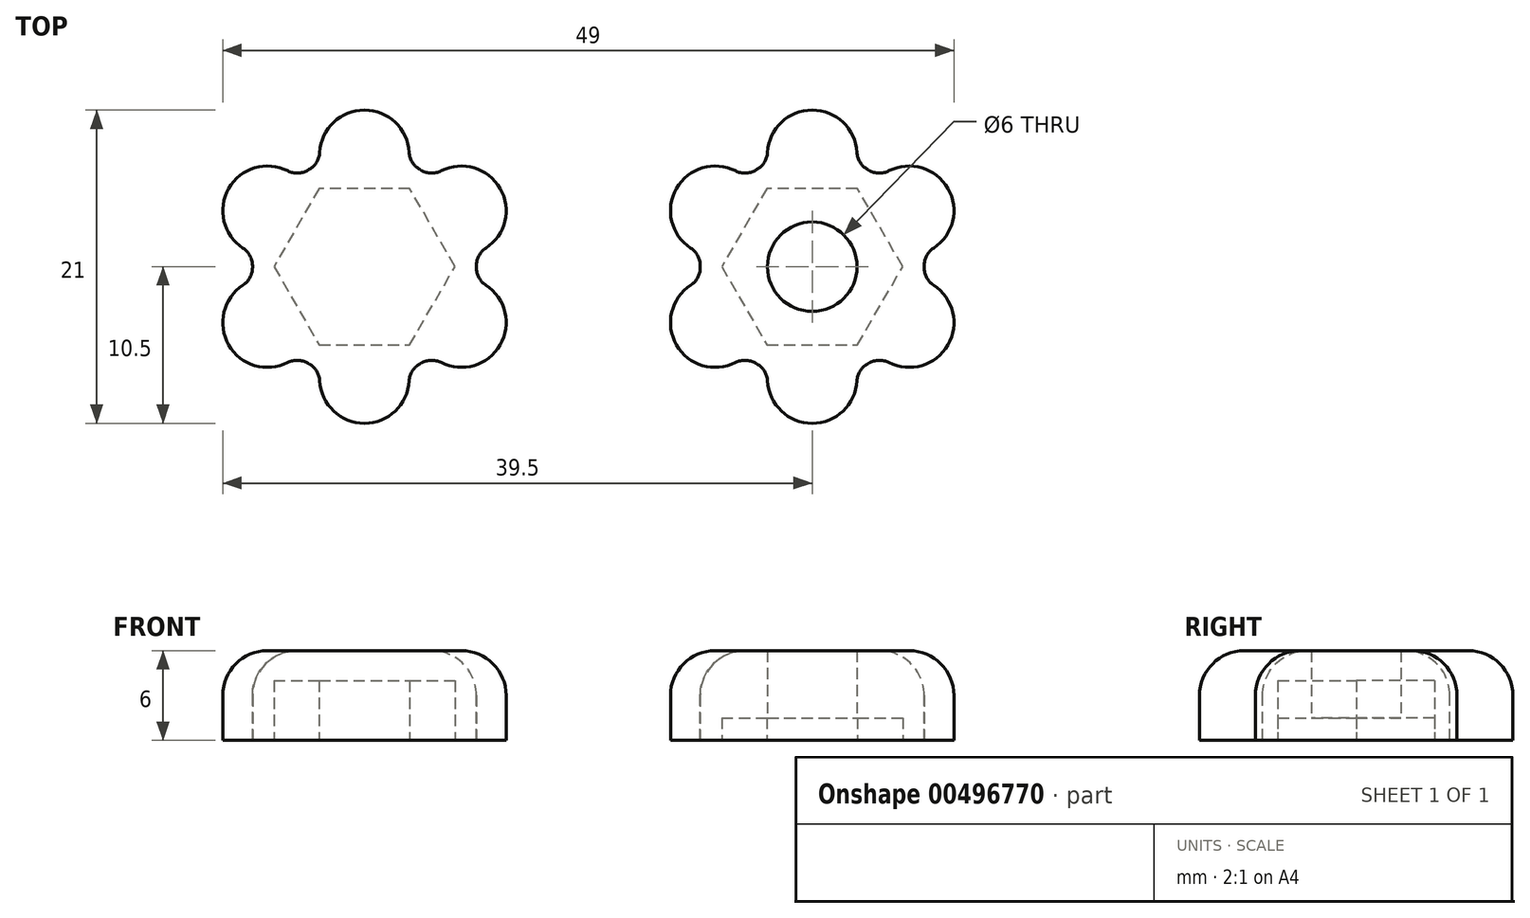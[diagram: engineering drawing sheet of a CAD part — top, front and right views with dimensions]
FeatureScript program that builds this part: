
annotation { "Feature Type Name" : "Feature", "Feature Type Description" : "" }
export const myFeature = defineFeature(function(context is Context, id is Id, definition is map)
    precondition{}
    {
        {
            var Q0;
            Q0=qCreatedBy(makeId("Top.planeOp"),FACE);
            var sketch = newSketch(context, id + "F0", { "sketchPlane" : qUnion([Q0])});
            skCircle(sketch, "E0", {"center": v(0, 0) * mm, "radius": 7.5 * mm});
            skCircle(sketch, "E1", {"center": v(0, 7.5) * mm, "radius": 3 * mm});
            skLineSegment(sketch, "E2", {"start": v(0, 0) * mm, "end": v(12.1, 6.98) * mm, "construction": true});
            skLineSegment(sketch, "E3", {"start": v(0, 0) * mm, "end": v(-10.24, 5.9) * mm, "construction": true});
            skLineSegment(sketch, "E4", {"start": v(-8.4, -4.85) * mm, "end": v(0, 0) * mm, "construction": true});
            skLineSegment(sketch, "E5", {"start": v(0, 0) * mm, "end": v(9.75, -5.63) * mm, "construction": true});
            skCircle(sketch, "E6", {"center": v(6.5, 3.75) * mm, "radius": 3 * mm});
            skCircle(sketch, "E7", {"center": v(6.5, -3.75) * mm, "radius": 3 * mm});
            skCircle(sketch, "E8", {"center": v(0, -7.5) * mm, "radius": 3 * mm});
            skCircle(sketch, "E9", {"center": v(-6.5, -3.75) * mm, "radius": 3 * mm});
            skCircle(sketch, "E10", {"center": v(-6.5, 3.75) * mm, "radius": 3 * mm});
            skSolve(sketch);
        }
        {
            var Q0;
            {var subQ0=sQuery(id+"F0.wireOp",EDGE,"E6");var subQ1=sQuery(id+"F0.wireOp",EDGE,"E0");var subQ11=makeQuery(id+"F0.imprint","INTERSECT",VERTEX,{"disambiguationData":[OD(0.0)],"derivedFrom":[subQ1,subQ0]});Q0=makeQuery(id+"F0.imprint","IMPRINT",FACE,{"disambiguationData":[TD([[makeQuery(id+"F0.imprint","IMPRINT",EDGE,{"disambiguationData":[TD([[subQ11,-1.0]])],"derivedFrom":subQ1}),1.0]])]});}
            var Q1;
            {var subQ0=sQuery(id+"F0.wireOp",EDGE,"E10");var subQ1=sQuery(id+"F0.wireOp",EDGE,"E0");var subQ2=makeQuery(id+"F0.imprint","INTERSECT",VERTEX,{"disambiguationData":[OD(0.0)],"derivedFrom":[subQ1,subQ0]});Q1=makeQuery(id+"F0.imprint","IMPRINT",FACE,{"disambiguationData":[TD([[makeQuery(id+"F0.imprint","IMPRINT",EDGE,{"disambiguationData":[TD([[subQ2,-1.0]])],"derivedFrom":subQ1}),1.0]])]});}
            var Q2;
            {var subQ0=sQuery(id+"F0.wireOp",EDGE,"E10");var subQ1=sQuery(id+"F0.wireOp",EDGE,"E0");var subQ2=makeQuery(id+"F0.imprint","INTERSECT",VERTEX,{"disambiguationData":[OD(0.0)],"derivedFrom":[subQ1,subQ0]});Q2=makeQuery(id+"F0.imprint","IMPRINT",FACE,{"disambiguationData":[TD([[makeQuery(id+"F0.imprint","IMPRINT",EDGE,{"disambiguationData":[TD([[subQ2,-1.0]])],"derivedFrom":subQ1}),-1.0]])]});}
            var Q3;
            {var subQ0=sQuery(id+"F0.wireOp",EDGE,"E1");var subQ1=sQuery(id+"F0.wireOp",EDGE,"E0");var subQ2=makeQuery(id+"F0.imprint","INTERSECT",VERTEX,{"disambiguationData":[OD(0.0)],"derivedFrom":[subQ1,subQ0]});Q3=makeQuery(id+"F0.imprint","IMPRINT",FACE,{"disambiguationData":[TD([[makeQuery(id+"F0.imprint","IMPRINT",EDGE,{"disambiguationData":[TD([[subQ2,-1.0]])],"derivedFrom":subQ1}),1.0]])]});}
            var Q4;
            {var subQ0=sQuery(id+"F0.wireOp",EDGE,"E6");var subQ1=sQuery(id+"F0.wireOp",EDGE,"E0");var subQ2=makeQuery(id+"F0.imprint","INTERSECT",VERTEX,{"disambiguationData":[OD(0.0)],"derivedFrom":[subQ1,subQ0]});Q4=makeQuery(id+"F0.imprint","IMPRINT",FACE,{"disambiguationData":[TD([[makeQuery(id+"F0.imprint","IMPRINT",EDGE,{"disambiguationData":[TD([[subQ2,1.0]])],"derivedFrom":subQ1}),1.0]])]});}
            var Q5;
            {var subQ0=sQuery(id+"F0.wireOp",EDGE,"E7");var subQ1=sQuery(id+"F0.wireOp",EDGE,"E0");var subQ2=makeQuery(id+"F0.imprint","INTERSECT",VERTEX,{"disambiguationData":[OD(0.0)],"derivedFrom":[subQ1,subQ0]});Q5=makeQuery(id+"F0.imprint","IMPRINT",FACE,{"disambiguationData":[TD([[makeQuery(id+"F0.imprint","IMPRINT",EDGE,{"disambiguationData":[TD([[subQ2,-1.0]])],"derivedFrom":subQ1}),1.0]])]});}
            var Q6;
            {var subQ0=sQuery(id+"F0.wireOp",EDGE,"E8");var subQ1=sQuery(id+"F0.wireOp",EDGE,"E0");var subQ2=makeQuery(id+"F0.imprint","INTERSECT",VERTEX,{"disambiguationData":[OD(0.0)],"derivedFrom":[subQ1,subQ0]});Q6=makeQuery(id+"F0.imprint","IMPRINT",FACE,{"disambiguationData":[TD([[makeQuery(id+"F0.imprint","IMPRINT",EDGE,{"disambiguationData":[TD([[subQ2,-1.0]])],"derivedFrom":subQ1}),1.0]])]});}
            var Q7;
            {var subQ0=sQuery(id+"F0.wireOp",EDGE,"E9");var subQ1=sQuery(id+"F0.wireOp",EDGE,"E0");var subQ2=makeQuery(id+"F0.imprint","INTERSECT",VERTEX,{"disambiguationData":[OD(0.0)],"derivedFrom":[subQ1,subQ0]});Q7=makeQuery(id+"F0.imprint","IMPRINT",FACE,{"disambiguationData":[TD([[makeQuery(id+"F0.imprint","IMPRINT",EDGE,{"disambiguationData":[TD([[subQ2,-1.0]])],"derivedFrom":subQ1}),1.0]])]});}
            var Q8;
            {var subQ0=sQuery(id+"F0.wireOp",EDGE,"E9");var subQ1=sQuery(id+"F0.wireOp",EDGE,"E0");var subQ2=makeQuery(id+"F0.imprint","INTERSECT",VERTEX,{"disambiguationData":[OD(0.0)],"derivedFrom":[subQ1,subQ0]});Q8=makeQuery(id+"F0.imprint","IMPRINT",FACE,{"disambiguationData":[TD([[makeQuery(id+"F0.imprint","IMPRINT",EDGE,{"disambiguationData":[TD([[subQ2,-1.0]])],"derivedFrom":subQ1}),-1.0]])]});}
            var Q9;
            {var subQ0=sQuery(id+"F0.wireOp",EDGE,"E8");var subQ1=sQuery(id+"F0.wireOp",EDGE,"E0");var subQ2=makeQuery(id+"F0.imprint","INTERSECT",VERTEX,{"disambiguationData":[OD(0.0)],"derivedFrom":[subQ1,subQ0]});Q9=makeQuery(id+"F0.imprint","IMPRINT",FACE,{"disambiguationData":[TD([[makeQuery(id+"F0.imprint","IMPRINT",EDGE,{"disambiguationData":[TD([[subQ2,-1.0]])],"derivedFrom":subQ1}),-1.0]])]});}
            var Q10;
            {var subQ0=sQuery(id+"F0.wireOp",EDGE,"E7");var subQ1=sQuery(id+"F0.wireOp",EDGE,"E0");var subQ2=makeQuery(id+"F0.imprint","INTERSECT",VERTEX,{"disambiguationData":[OD(0.0)],"derivedFrom":[subQ1,subQ0]});Q10=makeQuery(id+"F0.imprint","IMPRINT",FACE,{"disambiguationData":[TD([[makeQuery(id+"F0.imprint","IMPRINT",EDGE,{"disambiguationData":[TD([[subQ2,-1.0]])],"derivedFrom":subQ1}),-1.0]])]});}
            var Q11;
            {var subQ0=sQuery(id+"F0.wireOp",EDGE,"E6");var subQ1=sQuery(id+"F0.wireOp",EDGE,"E0");var subQ2=makeQuery(id+"F0.imprint","INTERSECT",VERTEX,{"disambiguationData":[OD(0.0)],"derivedFrom":[subQ1,subQ0]});Q11=makeQuery(id+"F0.imprint","IMPRINT",FACE,{"disambiguationData":[TD([[makeQuery(id+"F0.imprint","IMPRINT",EDGE,{"disambiguationData":[TD([[subQ2,1.0]])],"derivedFrom":subQ1}),-1.0]])]});}
            var Q12;
            {var subQ0=sQuery(id+"F0.wireOp",EDGE,"E1");var subQ1=sQuery(id+"F0.wireOp",EDGE,"E0");var subQ2=makeQuery(id+"F0.imprint","INTERSECT",VERTEX,{"disambiguationData":[OD(0.0)],"derivedFrom":[subQ1,subQ0]});Q12=makeQuery(id+"F0.imprint","IMPRINT",FACE,{"disambiguationData":[TD([[makeQuery(id+"F0.imprint","IMPRINT",EDGE,{"disambiguationData":[TD([[subQ2,-1.0]])],"derivedFrom":subQ1}),-1.0]])]});}
            extrude(context, id + "F1", {"entities" : qUnion([Q0, Q1, Q2, Q3, Q4, Q5, Q6, Q7, Q8, Q9, Q10, Q11, Q12]), "depth" : 6 * mm});
        }
        {
            var Q0;
            {var subQ0=sQuery(id+"F0.wireOp",EDGE,"E8");var subQ1=sQuery(id+"F0.wireOp",EDGE,"E0");Q0=makeQuery(id+"F1.opExtrude","SWEPT_EDGE",EDGE,{"disambiguationData":[OSD([subQ1,subQ0]),TDD([makeQuery(id+"F0.imprint","INTERSECT",VERTEX,{"disambiguationData":[OD(1.0)],"derivedFrom":[subQ1,subQ0]})])]});}
            var Q1;
            {var subQ0=sQuery(id+"F0.wireOp",EDGE,"E7");var subQ1=sQuery(id+"F0.wireOp",EDGE,"E0");Q1=makeQuery(id+"F1.opExtrude","SWEPT_EDGE",EDGE,{"disambiguationData":[OSD([subQ1,subQ0]),TDD([makeQuery(id+"F0.imprint","INTERSECT",VERTEX,{"disambiguationData":[OD(0.0)],"derivedFrom":[subQ1,subQ0]})])]});}
            var Q2;
            {var subQ0=sQuery(id+"F0.wireOp",EDGE,"E6");var subQ1=sQuery(id+"F0.wireOp",EDGE,"E0");Q2=makeQuery(id+"F1.opExtrude","SWEPT_EDGE",EDGE,{"disambiguationData":[OSD([subQ1,subQ0]),TDD([makeQuery(id+"F0.imprint","INTERSECT",VERTEX,{"disambiguationData":[OD(1.0)],"derivedFrom":[subQ1,subQ0]})])]});}
            var Q3;
            {var subQ0=sQuery(id+"F0.wireOp",EDGE,"E7");var subQ1=sQuery(id+"F0.wireOp",EDGE,"E0");Q3=makeQuery(id+"F1.opExtrude","SWEPT_EDGE",EDGE,{"disambiguationData":[OSD([subQ1,subQ0]),TDD([makeQuery(id+"F0.imprint","INTERSECT",VERTEX,{"disambiguationData":[OD(1.0)],"derivedFrom":[subQ1,subQ0]})])]});}
            var Q4;
            {var subQ0=sQuery(id+"F0.wireOp",EDGE,"E6");var subQ1=sQuery(id+"F0.wireOp",EDGE,"E0");Q4=makeQuery(id+"F1.opExtrude","SWEPT_EDGE",EDGE,{"disambiguationData":[OSD([subQ1,subQ0]),TDD([makeQuery(id+"F0.imprint","INTERSECT",VERTEX,{"disambiguationData":[OD(0.0)],"derivedFrom":[subQ1,subQ0]})])]});}
            var Q5;
            {var subQ0=sQuery(id+"F0.wireOp",EDGE,"E1");var subQ1=sQuery(id+"F0.wireOp",EDGE,"E0");Q5=makeQuery(id+"F1.opExtrude","SWEPT_EDGE",EDGE,{"disambiguationData":[OSD([subQ1,subQ0]),TDD([makeQuery(id+"F0.imprint","INTERSECT",VERTEX,{"disambiguationData":[OD(0.0)],"derivedFrom":[subQ1,subQ0]})])]});}
            var Q6;
            {var subQ0=sQuery(id+"F0.wireOp",EDGE,"E1");var subQ1=sQuery(id+"F0.wireOp",EDGE,"E0");Q6=makeQuery(id+"F1.opExtrude","SWEPT_EDGE",EDGE,{"disambiguationData":[OSD([subQ1,subQ0]),TDD([makeQuery(id+"F0.imprint","INTERSECT",VERTEX,{"disambiguationData":[OD(1.0)],"derivedFrom":[subQ1,subQ0]})])]});}
            var Q7;
            {var subQ0=sQuery(id+"F0.wireOp",EDGE,"E10");var subQ1=sQuery(id+"F0.wireOp",EDGE,"E0");Q7=makeQuery(id+"F1.opExtrude","SWEPT_EDGE",EDGE,{"disambiguationData":[OSD([subQ1,subQ0]),TDD([makeQuery(id+"F0.imprint","INTERSECT",VERTEX,{"disambiguationData":[OD(0.0)],"derivedFrom":[subQ1,subQ0]})])]});}
            var Q8;
            {var subQ0=sQuery(id+"F0.wireOp",EDGE,"E10");var subQ1=sQuery(id+"F0.wireOp",EDGE,"E0");Q8=makeQuery(id+"F1.opExtrude","SWEPT_EDGE",EDGE,{"disambiguationData":[OSD([subQ1,subQ0]),TDD([makeQuery(id+"F0.imprint","INTERSECT",VERTEX,{"disambiguationData":[OD(1.0)],"derivedFrom":[subQ1,subQ0]})])]});}
            var Q9;
            {var subQ0=sQuery(id+"F0.wireOp",EDGE,"E9");var subQ1=sQuery(id+"F0.wireOp",EDGE,"E0");Q9=makeQuery(id+"F1.opExtrude","SWEPT_EDGE",EDGE,{"disambiguationData":[OSD([subQ1,subQ0]),TDD([makeQuery(id+"F0.imprint","INTERSECT",VERTEX,{"disambiguationData":[OD(0.0)],"derivedFrom":[subQ1,subQ0]})])]});}
            var Q10;
            {var subQ0=sQuery(id+"F0.wireOp",EDGE,"E9");var subQ1=sQuery(id+"F0.wireOp",EDGE,"E0");Q10=makeQuery(id+"F1.opExtrude","SWEPT_EDGE",EDGE,{"disambiguationData":[OSD([subQ1,subQ0]),TDD([makeQuery(id+"F0.imprint","INTERSECT",VERTEX,{"disambiguationData":[OD(1.0)],"derivedFrom":[subQ1,subQ0]})])]});}
            var Q11;
            {var subQ0=sQuery(id+"F0.wireOp",EDGE,"E8");var subQ1=sQuery(id+"F0.wireOp",EDGE,"E0");Q11=makeQuery(id+"F1.opExtrude","SWEPT_EDGE",EDGE,{"disambiguationData":[OSD([subQ1,subQ0]),TDD([makeQuery(id+"F0.imprint","INTERSECT",VERTEX,{"disambiguationData":[OD(0.0)],"derivedFrom":[subQ1,subQ0]})])]});}
            fillet(context, id + "F2", {"entities" : qUnion([Q0, Q1, Q2, Q3, Q4, Q5, Q6, Q7, Q8, Q9, Q10, Q11]), "radius" : 1.4 * mm, "tangentPropagation" : true, "allowEdgeOverflow" : false});
        }
        {
            var Q0;
            Q0=makeQuery(id+"F1.opExtrude","CAP_EDGE",EDGE,{"disambiguationData":[OSD([sQuery(id+"F0.wireOp",EDGE,"E8")])],"isStart":false});
            fillet(context, id + "F3", {"entities" : qUnion([Q0]), "radius" : 3 * mm, "tangentPropagation" : true, "allowEdgeOverflow" : false});
        }
        {
            var Q0;
            Q0=makeQuery(id+"F1.opExtrude","SWEPT_BODY",BODY,{"disambiguationData":[OSD([sQuery(id+"F0.wireOp",EDGE,"E0"),sQuery(id+"F0.wireOp",EDGE,"E1"),sQuery(id+"F0.wireOp",EDGE,"E6"),sQuery(id+"F0.wireOp",EDGE,"E7"),sQuery(id+"F0.wireOp",EDGE,"E8"),sQuery(id+"F0.wireOp",EDGE,"E9"),sQuery(id+"F0.wireOp",EDGE,"E10")])]});
            transform(context, id + "F4", {"entities" : qUnion([Q0]), "transformType" : TransformType.TRANSLATION_3D, "dx" : 30 * mm, "dy" : 0 * mm, "dz" : 0 * mm, "makeCopy" : true});
        }
        {
            var Q0;
            Q0=makeQuery(id+"F1.opExtrude","CAP_FACE",FACE,{"disambiguationData":[OSD([sQuery(id+"F0.wireOp",EDGE,"E0"),sQuery(id+"F0.wireOp",EDGE,"E1"),sQuery(id+"F0.wireOp",EDGE,"E6"),sQuery(id+"F0.wireOp",EDGE,"E7"),sQuery(id+"F0.wireOp",EDGE,"E8"),sQuery(id+"F0.wireOp",EDGE,"E9"),sQuery(id+"F0.wireOp",EDGE,"E10")])],"isStart":true});
            var sketch = newSketch(context, id + "F5", { "sketchPlane" : qUnion([Q0])});
            skCircle(sketch, "E11.cCircle", {"center": v(0, 0) * mm, "radius": 5.25 * mm, "construction": true});
            skLineSegment(sketch, "E11.0", {"start": v(3.03, 5.25) * mm, "end": v(6.06, 0) * mm});
            skLineSegment(sketch, "E11.1", {"start": v(6.06, 0) * mm, "end": v(3.03, -5.25) * mm});
            skLineSegment(sketch, "E11.2", {"start": v(3.03, -5.25) * mm, "end": v(-3.03, -5.25) * mm});
            skLineSegment(sketch, "E11.3", {"start": v(-3.03, -5.25) * mm, "end": v(-6.06, 0) * mm});
            skLineSegment(sketch, "E11.4", {"start": v(-6.06, 0) * mm, "end": v(-3.03, 5.25) * mm});
            skLineSegment(sketch, "E11.5", {"start": v(-3.03, 5.25) * mm, "end": v(3.03, 5.25) * mm});
            skPoint(sketch, "E11.0.midPoint", {"position": v(4.55, 2.62) * mm});
            skSolve(sketch);
        }
        {
            var Q0;
            Q0=makeQuery(id+"F5.imprint","IMPRINT",FACE,{"disambiguationData":[TD([[makeQuery(id+"F5.imprint","IMPRINT",EDGE,{"derivedFrom":sQuery(id+"F5.wireOp",EDGE,"E11.0")}),-1.0]])]});
            extrude(context, id + "F6", {"entities" : qUnion([Q0]), "operationType" : NewBodyOperationType.REMOVE, "oppositeDirection" : true, "depth" : 4 * mm});
        }
        {
            var Q0;
            Q0=makeQuery(id+"F4.opPattern","COPY",FACE,{"derivedFrom":makeQuery(id+"F1.opExtrude","CAP_FACE",FACE,{"disambiguationData":[OSD([sQuery(id+"F0.wireOp",EDGE,"E0"),sQuery(id+"F0.wireOp",EDGE,"E1"),sQuery(id+"F0.wireOp",EDGE,"E6"),sQuery(id+"F0.wireOp",EDGE,"E7"),sQuery(id+"F0.wireOp",EDGE,"E8"),sQuery(id+"F0.wireOp",EDGE,"E9"),sQuery(id+"F0.wireOp",EDGE,"E10")])],"isStart":true}),"instanceName":"1"});
            var sketch = newSketch(context, id + "F7", { "sketchPlane" : qUnion([Q0])});
            skCircle(sketch, "E12.cCircle", {"center": v(30, 0) * mm, "radius": 5.25 * mm, "construction": true});
            skLineSegment(sketch, "E12.0", {"start": v(33.03, 5.25) * mm, "end": v(36.06, 0) * mm});
            skLineSegment(sketch, "E12.1", {"start": v(36.06, 0) * mm, "end": v(33.03, -5.25) * mm});
            skLineSegment(sketch, "E12.2", {"start": v(33.03, -5.25) * mm, "end": v(26.97, -5.25) * mm});
            skLineSegment(sketch, "E12.3", {"start": v(26.97, -5.25) * mm, "end": v(23.94, 0) * mm});
            skLineSegment(sketch, "E12.4", {"start": v(23.94, 0) * mm, "end": v(26.97, 5.25) * mm});
            skLineSegment(sketch, "E12.5", {"start": v(26.97, 5.25) * mm, "end": v(33.03, 5.25) * mm});
            skPoint(sketch, "E12.0.midPoint", {"position": v(34.55, 2.62) * mm});
            skSolve(sketch);
        }
        {
            var Q0;
            Q0=makeQuery(id+"F7.imprint","IMPRINT",FACE,{"disambiguationData":[TD([[makeQuery(id+"F7.imprint","IMPRINT",EDGE,{"derivedFrom":sQuery(id+"F7.wireOp",EDGE,"E12.0")}),-1.0]])]});
            extrude(context, id + "F8", {"entities" : qUnion([Q0]), "operationType" : NewBodyOperationType.REMOVE, "oppositeDirection" : true, "depth" : 1.5 * mm});
        }
        {
            var Q0;
            Q0=makeQuery(id+"F8.boolean.opBoolean","COPY",FACE,{"derivedFrom":makeQuery(id+"F8.opExtrude","CAP_FACE",FACE,{"disambiguationData":[OSD([sQuery(id+"F7.wireOp",EDGE,"E12.0"),sQuery(id+"F7.wireOp",EDGE,"E12.1"),sQuery(id+"F7.wireOp",EDGE,"E12.2"),sQuery(id+"F7.wireOp",EDGE,"E12.3"),sQuery(id+"F7.wireOp",EDGE,"E12.4"),sQuery(id+"F7.wireOp",EDGE,"E12.5")])],"isStart":false})});
            var sketch = newSketch(context, id + "F9", { "sketchPlane" : qUnion([Q0])});
            skCircle(sketch, "E13", {"center": v(30, 0) * mm, "radius": 3 * mm});
            skSolve(sketch);
        }
        {
            var Q0;
            Q0=makeQuery(id+"F9.imprint","IMPRINT",FACE,{"disambiguationData":[TD([[makeQuery(id+"F9.imprint","IMPRINT",EDGE,{"derivedFrom":sQuery(id+"F9.wireOp",EDGE,"E13")}),1.0]])]});
            extrude(context, id + "F10", {"entities" : qUnion([Q0]), "operationType" : NewBodyOperationType.REMOVE, "endBound" : BoundingType.THROUGH_ALL, "oppositeDirection" : true, "depth" : 25 * mm});
        }
    });
